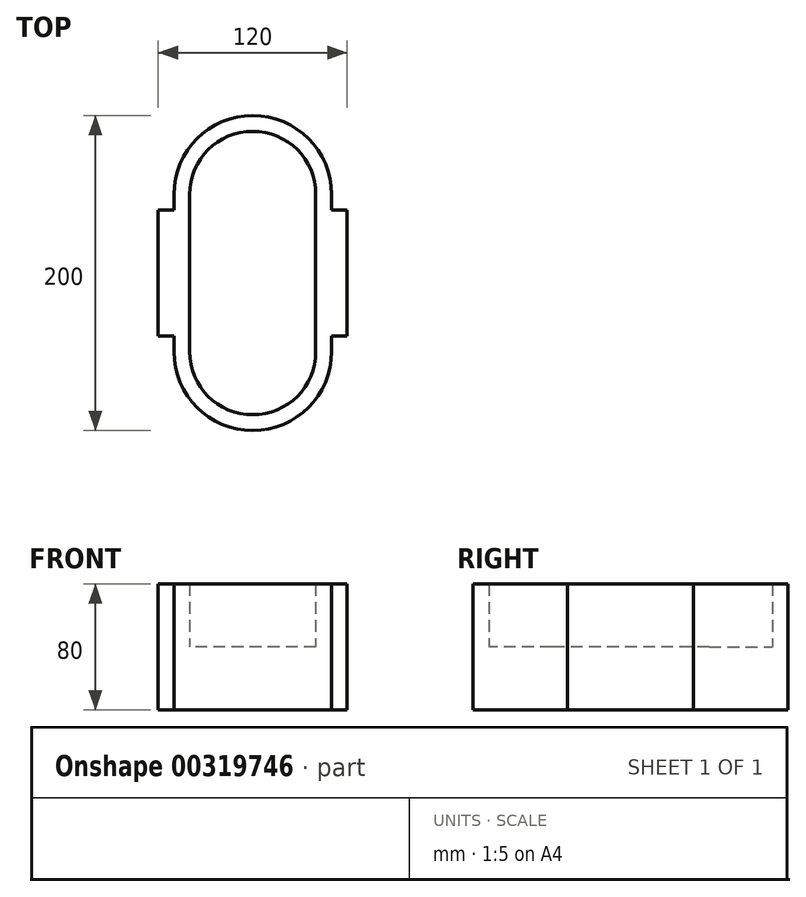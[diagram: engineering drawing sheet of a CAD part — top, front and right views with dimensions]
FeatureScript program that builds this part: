
annotation { "Feature Type Name" : "Feature", "Feature Type Description" : "" }
export const myFeature = defineFeature(function(context is Context, id is Id, definition is map)
    precondition{}
    {
        {
            var Q0;
            Q0=qCreatedBy(makeId("Top.planeOp"),FACE);
            var sketch = newSketch(context, id + "F0", { "sketchPlane" : qUnion([Q0])});
            skLineSegment(sketch, "E0.left", {"start": v(-50, 50) * mm, "end": v(-50, -50) * mm});
            skLineSegment(sketch, "E0.right", {"start": v(50, 50) * mm, "end": v(50, -50) * mm});
            skArc(sketch, "E1", {"start": v(-50, -50) * mm, "mid": v(0, -100) * mm, "end": v(50, -50) * mm});
            skArc(sketch, "E2", {"start": v(50, 50) * mm, "mid": v(0, 100) * mm, "end": v(-50, 50) * mm});
            skLineSegment(sketch, "E3.left", {"start": v(-40, 50) * mm, "end": v(-40, -50) * mm});
            skLineSegment(sketch, "E3.right", {"start": v(40, 50) * mm, "end": v(40, -50) * mm});
            skArc(sketch, "E4", {"start": v(40, 50) * mm, "mid": v(0, 90) * mm, "end": v(-40, 50) * mm});
            skArc(sketch, "E5", {"start": v(-40, -50) * mm, "mid": v(0, -90) * mm, "end": v(40, -50) * mm});
            skPoint(sketch, "E6", {"position": v(-40, 0) * mm});
            skPoint(sketch, "E7", {"position": v(40, 0) * mm});
            skLineSegment(sketch, "E8.bottom", {"start": v(-60, 40) * mm, "end": v(-50, 40) * mm});
            skLineSegment(sketch, "E8.top", {"start": v(-60, -40) * mm, "end": v(-50, -40) * mm});
            skLineSegment(sketch, "E8.left", {"start": v(-60, 40) * mm, "end": v(-60, -40) * mm});
            skLineSegment(sketch, "E8.right", {"start": v(-50, 40) * mm, "end": v(-50, -40) * mm});
            skPoint(sketch, "E9", {"position": v(-50, 0) * mm});
            skPoint(sketch, "E10", {"position": v(50, 0) * mm});
            skPoint(sketch, "E11", {"position": v(0, -90) * mm});
            skPoint(sketch, "E12", {"position": v(0, -100) * mm});
            skPoint(sketch, "E13", {"position": v(0, 90) * mm});
            skPoint(sketch, "E14", {"position": v(0, 100) * mm});
            skLineSegment(sketch, "E15.bottom", {"start": v(50, 40) * mm, "end": v(60, 40) * mm});
            skLineSegment(sketch, "E15.top", {"start": v(50, -40) * mm, "end": v(60, -40) * mm});
            skLineSegment(sketch, "E15.left", {"start": v(50, 40) * mm, "end": v(50, -40) * mm});
            skLineSegment(sketch, "E15.right", {"start": v(60, 40) * mm, "end": v(60, -40) * mm});
            skSolve(sketch);
        }
        {
            var Q0;
            {var subQ1=sQuery(id+"F0.wireOp",EDGE,"E1");Q0=makeQuery(id+"F0.imprint","IMPRINT",FACE,{"disambiguationData":[TD([[makeQuery(id+"F0.imprint","IMPRINT",EDGE,{"derivedFrom":subQ1}),1.0]])]});}
            extrude(context, id + "F1", {"entities" : qUnion([Q0]), "depth" : 80 * mm});
        }
        {
            var Q0;
            Q0=makeQuery(id+"F0.imprint","IMPRINT",FACE,{"disambiguationData":[TD([[makeQuery(id+"F0.imprint","IMPRINT",EDGE,{"derivedFrom":sQuery(id+"F0.wireOp",EDGE,"E3.left")}),1.0]])]});
            extrude(context, id + "F2", {"entities" : qUnion([Q0]), "operationType" : NewBodyOperationType.ADD, "depth" : 40 * mm});
        }
        {
            var Q0;
            Q0=makeQuery(id+"F0.imprint","IMPRINT",FACE,{"disambiguationData":[TD([[makeQuery(id+"F0.imprint","IMPRINT",EDGE,{"derivedFrom":sQuery(id+"F0.wireOp",EDGE,"E15.bottom")}),-1.0]])]});
            var Q1;
            Q1=makeQuery(id+"F0.imprint","IMPRINT",FACE,{"disambiguationData":[TD([[makeQuery(id+"F0.imprint","IMPRINT",EDGE,{"derivedFrom":sQuery(id+"F0.wireOp",EDGE,"E8.bottom")}),-1.0]])]});
            extrude(context, id + "F3", {"entities" : qUnion([Q0, Q1]), "operationType" : NewBodyOperationType.ADD, "depth" : 80 * mm});
        }
    });
